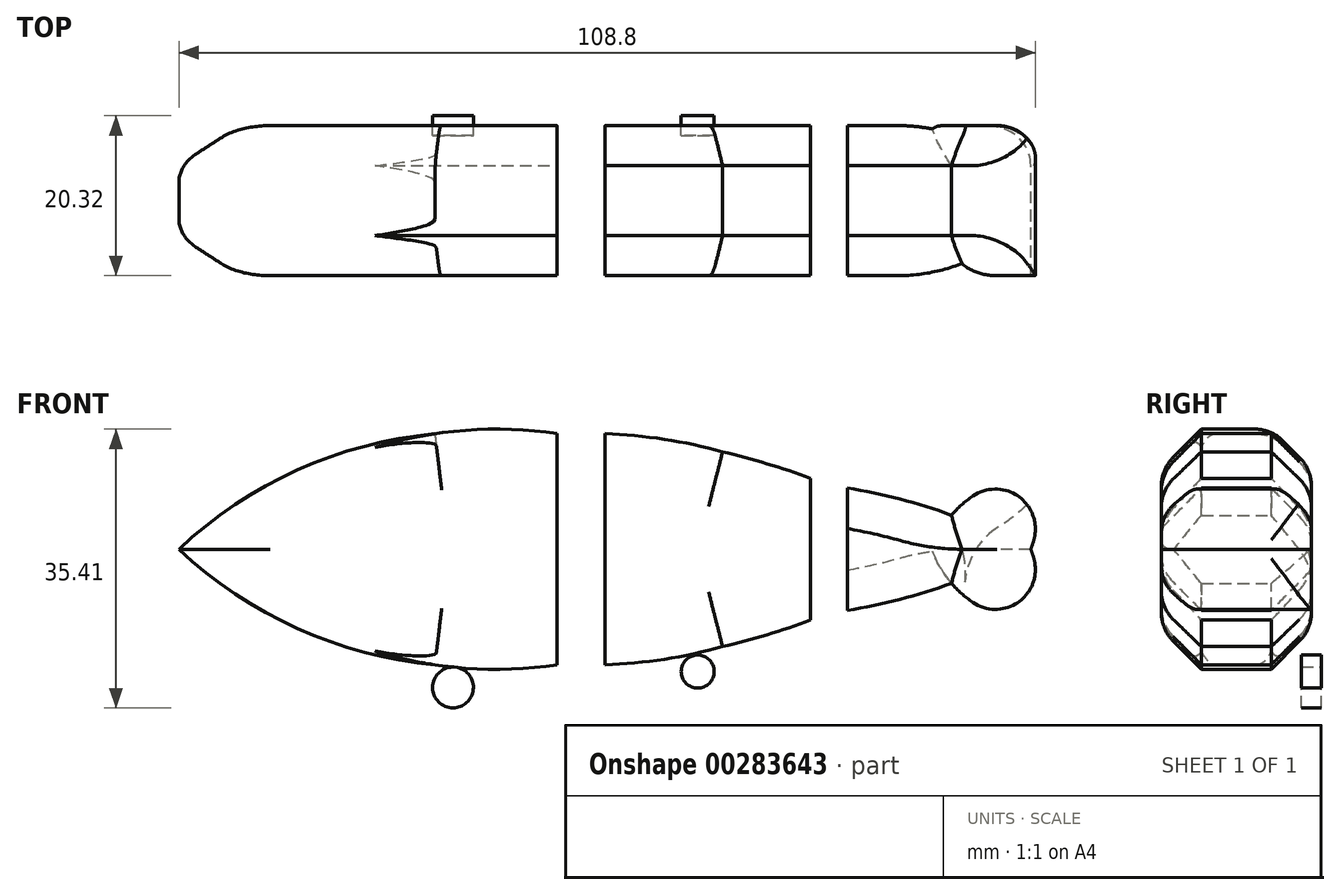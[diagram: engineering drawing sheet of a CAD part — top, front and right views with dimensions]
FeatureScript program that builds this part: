
annotation { "Feature Type Name" : "Feature", "Feature Type Description" : "" }
export const myFeature = defineFeature(function(context is Context, id is Id, definition is map)
    precondition{}
    {
        {
            var Q0;
            Q0=qCreatedBy(makeId("Front.planeOp"),FACE);
            var sketch = newSketch(context, id + "F0", { "sketchPlane" : qUnion([Q0])});
            skArc(sketch, "E0", {"start": v(-18.42, 14.68) * mm, "mid": v(-35.9, 10.05) * mm, "end": v(-50.94, 0) * mm});
            skArc(sketch, "E1", {"start": v(-2.88, 14.68) * mm, "mid": v(-10.65, 15.26) * mm, "end": v(-18.42, 14.68) * mm});
            skArc(sketch, "E2", {"start": v(18.13, 12.38) * mm, "mid": v(10.72, 13.97) * mm, "end": v(3.17, 14.68) * mm});
            skArc(sketch, "E3", {"start": v(29.31, 9) * mm, "mid": v(23.77, 10.86) * mm, "end": v(18.13, 12.38) * mm});
            skLineSegment(sketch, "E4", {"start": v(-2.88, 14.68) * mm, "end": v(-2.88, 0) * mm});
            skLineSegment(sketch, "E5", {"start": v(3.17, 14.68) * mm, "end": v(3.17, 0) * mm});
            skArc(sketch, "E6.MirrorCS", {"start": v(-18.42, -14.68) * mm, "mid": v(-35.9, -10.05) * mm, "end": v(-50.94, 0) * mm});
            skArc(sketch, "E7.MirrorCS", {"start": v(-2.88, -14.68) * mm, "mid": v(-10.65, -15.26) * mm, "end": v(-18.42, -14.68) * mm});
            skLineSegment(sketch, "E8.MirrorCS", {"start": v(-2.88, -14.68) * mm, "end": v(-2.88, 0) * mm});
            skLineSegment(sketch, "E9.MirrorCS", {"start": v(3.17, -14.68) * mm, "end": v(3.17, 0) * mm});
            skArc(sketch, "E10.MirrorCS", {"start": v(18.13, -12.38) * mm, "mid": v(10.72, -13.97) * mm, "end": v(3.17, -14.68) * mm});
            skArc(sketch, "E11.MirrorCS", {"start": v(29.31, -9) * mm, "mid": v(23.77, -10.86) * mm, "end": v(18.13, -12.38) * mm});
            skLineSegment(sketch, "E12", {"start": v(29.31, 9) * mm, "end": v(29.31, -9) * mm});
            skPoint(sketch, "E13.orphan", {"position": v(40, 4.32) * mm});
            skPoint(sketch, "E14.orphan", {"position": v(40, -4.32) * mm});
            skArc(sketch, "E15", {"start": v(47.2, 4.32) * mm, "mid": v(40.67, 6.37) * mm, "end": v(33.96, 7.77) * mm});
            skLineSegment(sketch, "E16", {"start": v(33.96, 7.77) * mm, "end": v(33.96, 0) * mm});
            skArc(sketch, "E17", {"start": v(57.27, 9.2) * mm, "mid": v(51.73, 7.81) * mm, "end": v(47.2, 4.32) * mm});
            skArc(sketch, "E18", {"start": v(57.27, 0) * mm, "mid": v(58.14, 4.6) * mm, "end": v(57.27, 9.2) * mm});
            skArc(sketch, "E19.MirrorCS", {"start": v(47.2, -4.32) * mm, "mid": v(40.67, -6.37) * mm, "end": v(33.96, -7.77) * mm});
            skLineSegment(sketch, "E20.MirrorCS", {"start": v(33.96, -7.77) * mm, "end": v(33.96, 0) * mm});
            skArc(sketch, "E21.MirrorCS", {"start": v(57.27, -9.2) * mm, "mid": v(51.73, -7.81) * mm, "end": v(47.2, -4.32) * mm});
            skArc(sketch, "E22.MirrorCS", {"start": v(57.27, 0) * mm, "mid": v(58.14, -4.6) * mm, "end": v(57.27, -9.2) * mm});
            skSolve(sketch);
        }
        {
            var Q0;
            Q0=makeQuery(id+"F0.imprint","IMPRINT",FACE,{"disambiguationData":[TD([[makeQuery(id+"F0.imprint","IMPRINT",EDGE,{"derivedFrom":sQuery(id+"F0.wireOp",EDGE,"E2")}),1.0]])]});
            var Q1;
            Q1=makeQuery(id+"F0.imprint","IMPRINT",FACE,{"disambiguationData":[TD([[makeQuery(id+"F0.imprint","IMPRINT",EDGE,{"derivedFrom":sQuery(id+"F0.wireOp",EDGE,"E15")}),1.0]])]});
            var Q2;
            Q2=makeQuery(id+"F0.imprint","IMPRINT",FACE,{"disambiguationData":[TD([[makeQuery(id+"F0.imprint","IMPRINT",EDGE,{"derivedFrom":sQuery(id+"F0.wireOp",EDGE,"E0")}),1.0]])]});
            extrude(context, id + "F1", {"entities" : qUnion([Q0, Q1, Q2]), "depth" : 19.05 * mm});
        }
        {
            var Q0;
            Q0=makeQuery(id+"F1.opExtrude","CAP_EDGE",EDGE,{"disambiguationData":[OSD([sQuery(id+"F0.wireOp",EDGE,"E0")])],"isStart":false});
            var Q1;
            Q1=makeQuery(id+"F1.opExtrude","CAP_EDGE",EDGE,{"disambiguationData":[OSD([sQuery(id+"F0.wireOp",EDGE,"E1")])],"isStart":false});
            var Q2;
            Q2=makeQuery(id+"F1.opExtrude","CAP_EDGE",EDGE,{"disambiguationData":[OSD([sQuery(id+"F0.wireOp",EDGE,"E6.MirrorCS")])],"isStart":false});
            var Q3;
            Q3=makeQuery(id+"F1.opExtrude","CAP_EDGE",EDGE,{"disambiguationData":[OSD([sQuery(id+"F0.wireOp",EDGE,"E7.MirrorCS")])],"isStart":false});
            var Q4;
            Q4=makeQuery(id+"F1.opExtrude","CAP_EDGE",EDGE,{"disambiguationData":[OSD([sQuery(id+"F0.wireOp",EDGE,"E1")])],"isStart":true});
            var Q5;
            Q5=makeQuery(id+"F1.opExtrude","CAP_EDGE",EDGE,{"disambiguationData":[OSD([sQuery(id+"F0.wireOp",EDGE,"E2")])],"isStart":true});
            var Q6;
            Q6=makeQuery(id+"F1.opExtrude","CAP_EDGE",EDGE,{"disambiguationData":[OSD([sQuery(id+"F0.wireOp",EDGE,"E3")])],"isStart":false});
            var Q7;
            Q7=makeQuery(id+"F1.opExtrude","CAP_EDGE",EDGE,{"disambiguationData":[OSD([sQuery(id+"F0.wireOp",EDGE,"E2")])],"isStart":false});
            var Q8;
            Q8=makeQuery(id+"F1.opExtrude","CAP_EDGE",EDGE,{"disambiguationData":[OSD([sQuery(id+"F0.wireOp",EDGE,"E15")])],"isStart":false});
            var Q9;
            Q9=makeQuery(id+"F1.opExtrude","CAP_EDGE",EDGE,{"disambiguationData":[OSD([sQuery(id+"F0.wireOp",EDGE,"E15")])],"isStart":true});
            var Q10;
            Q10=makeQuery(id+"F1.opExtrude","CAP_EDGE",EDGE,{"disambiguationData":[OSD([sQuery(id+"F0.wireOp",EDGE,"E17")])],"isStart":true});
            var Q11;
            Q11=makeQuery(id+"F1.opExtrude","CAP_EDGE",EDGE,{"disambiguationData":[OSD([sQuery(id+"F0.wireOp",EDGE,"E17")])],"isStart":false});
            var Q12;
            Q12=makeQuery(id+"F1.opExtrude","CAP_EDGE",EDGE,{"disambiguationData":[OSD([sQuery(id+"F0.wireOp",EDGE,"E21.MirrorCS")])],"isStart":false});
            var Q13;
            Q13=makeQuery(id+"F1.opExtrude","CAP_EDGE",EDGE,{"disambiguationData":[OSD([sQuery(id+"F0.wireOp",EDGE,"E19.MirrorCS")])],"isStart":false});
            var Q14;
            Q14=makeQuery(id+"F1.opExtrude","CAP_EDGE",EDGE,{"disambiguationData":[OSD([sQuery(id+"F0.wireOp",EDGE,"E10.MirrorCS")])],"isStart":false});
            var Q15;
            Q15=makeQuery(id+"F1.opExtrude","CAP_EDGE",EDGE,{"disambiguationData":[OSD([sQuery(id+"F0.wireOp",EDGE,"E19.MirrorCS")])],"isStart":true});
            var Q16;
            Q16=makeQuery(id+"F1.opExtrude","CAP_EDGE",EDGE,{"disambiguationData":[OSD([sQuery(id+"F0.wireOp",EDGE,"E6.MirrorCS")])],"isStart":true});
            var Q17;
            Q17=makeQuery(id+"F1.opExtrude","CAP_EDGE",EDGE,{"disambiguationData":[OSD([sQuery(id+"F0.wireOp",EDGE,"E7.MirrorCS")])],"isStart":true});
            var Q18;
            Q18=makeQuery(id+"F1.opExtrude","CAP_EDGE",EDGE,{"disambiguationData":[OSD([sQuery(id+"F0.wireOp",EDGE,"E10.MirrorCS")])],"isStart":true});
            chamfer(context, id + "F2", {"entities" : qUnion([Q0, Q1, Q2, Q3, Q4, Q5, Q6, Q7, Q8, Q9, Q10, Q11, Q12, Q13, Q14, Q15, Q16, Q17, Q18]), "width" : 5.08 * mm, "tangentPropagation" : true});
        }
        {
            var Q0;
            {var subQ0=sQuery(id+"F0.wireOp",EDGE,"E0");Q0=makeQuery(id+"F2.opChamfer","BLEND_EDGE",EDGE,{"blendedFrom":[makeQuery(id+"F1.opExtrude","CAP_EDGE",EDGE,{"disambiguationData":[OSD([subQ0])],"isStart":false}),makeQuery(id+"F1.opExtrude","CAP_FACE",FACE,{"disambiguationData":[OSD([subQ0,sQuery(id+"F0.wireOp",EDGE,"E1"),sQuery(id+"F0.wireOp",EDGE,"E4"),sQuery(id+"F0.wireOp",EDGE,"E6.MirrorCS"),sQuery(id+"F0.wireOp",EDGE,"E7.MirrorCS"),sQuery(id+"F0.wireOp",EDGE,"E8.MirrorCS")])],"isStart":false})],"blendedInto":[makeQuery(id+"F1.opExtrude","CAP_FACE",FACE,{"disambiguationData":[OSD([subQ0,sQuery(id+"F0.wireOp",EDGE,"E1"),sQuery(id+"F0.wireOp",EDGE,"E4"),sQuery(id+"F0.wireOp",EDGE,"E6.MirrorCS"),sQuery(id+"F0.wireOp",EDGE,"E7.MirrorCS"),sQuery(id+"F0.wireOp",EDGE,"E8.MirrorCS")])],"isStart":false})]});}
            var Q1;
            {var subQ0=sQuery(id+"F0.wireOp",EDGE,"E1");Q1=makeQuery(id+"F2.opChamfer","BLEND_EDGE",EDGE,{"blendedFrom":[makeQuery(id+"F1.opExtrude","CAP_EDGE",EDGE,{"disambiguationData":[OSD([subQ0])],"isStart":false}),makeQuery(id+"F1.opExtrude","CAP_FACE",FACE,{"disambiguationData":[OSD([sQuery(id+"F0.wireOp",EDGE,"E0"),subQ0,sQuery(id+"F0.wireOp",EDGE,"E4"),sQuery(id+"F0.wireOp",EDGE,"E6.MirrorCS"),sQuery(id+"F0.wireOp",EDGE,"E7.MirrorCS"),sQuery(id+"F0.wireOp",EDGE,"E8.MirrorCS")])],"isStart":false})],"blendedInto":[makeQuery(id+"F1.opExtrude","CAP_FACE",FACE,{"disambiguationData":[OSD([sQuery(id+"F0.wireOp",EDGE,"E0"),subQ0,sQuery(id+"F0.wireOp",EDGE,"E4"),sQuery(id+"F0.wireOp",EDGE,"E6.MirrorCS"),sQuery(id+"F0.wireOp",EDGE,"E7.MirrorCS"),sQuery(id+"F0.wireOp",EDGE,"E8.MirrorCS")])],"isStart":false})]});}
            var Q2;
            {var subQ0=sQuery(id+"F0.wireOp",EDGE,"E6.MirrorCS");Q2=makeQuery(id+"F2.opChamfer","BLEND_EDGE",EDGE,{"blendedFrom":[makeQuery(id+"F1.opExtrude","CAP_EDGE",EDGE,{"disambiguationData":[OSD([subQ0])],"isStart":false}),makeQuery(id+"F1.opExtrude","CAP_FACE",FACE,{"disambiguationData":[OSD([sQuery(id+"F0.wireOp",EDGE,"E0"),sQuery(id+"F0.wireOp",EDGE,"E1"),sQuery(id+"F0.wireOp",EDGE,"E4"),subQ0,sQuery(id+"F0.wireOp",EDGE,"E7.MirrorCS"),sQuery(id+"F0.wireOp",EDGE,"E8.MirrorCS")])],"isStart":false})],"blendedInto":[makeQuery(id+"F1.opExtrude","CAP_FACE",FACE,{"disambiguationData":[OSD([sQuery(id+"F0.wireOp",EDGE,"E0"),sQuery(id+"F0.wireOp",EDGE,"E1"),sQuery(id+"F0.wireOp",EDGE,"E4"),subQ0,sQuery(id+"F0.wireOp",EDGE,"E7.MirrorCS"),sQuery(id+"F0.wireOp",EDGE,"E8.MirrorCS")])],"isStart":false})]});}
            var Q3;
            {var subQ0=sQuery(id+"F0.wireOp",EDGE,"E7.MirrorCS");Q3=makeQuery(id+"F2.opChamfer","BLEND_EDGE",EDGE,{"blendedFrom":[makeQuery(id+"F1.opExtrude","CAP_EDGE",EDGE,{"disambiguationData":[OSD([subQ0])],"isStart":false}),makeQuery(id+"F1.opExtrude","CAP_FACE",FACE,{"disambiguationData":[OSD([sQuery(id+"F0.wireOp",EDGE,"E0"),sQuery(id+"F0.wireOp",EDGE,"E1"),sQuery(id+"F0.wireOp",EDGE,"E4"),sQuery(id+"F0.wireOp",EDGE,"E6.MirrorCS"),subQ0,sQuery(id+"F0.wireOp",EDGE,"E8.MirrorCS")])],"isStart":false})],"blendedInto":[makeQuery(id+"F1.opExtrude","CAP_FACE",FACE,{"disambiguationData":[OSD([sQuery(id+"F0.wireOp",EDGE,"E0"),sQuery(id+"F0.wireOp",EDGE,"E1"),sQuery(id+"F0.wireOp",EDGE,"E4"),sQuery(id+"F0.wireOp",EDGE,"E6.MirrorCS"),subQ0,sQuery(id+"F0.wireOp",EDGE,"E8.MirrorCS")])],"isStart":false})]});}
            var Q4;
            {var subQ0=sQuery(id+"F0.wireOp",EDGE,"E11.MirrorCS");Q4=makeQuery(id+"F2.opChamfer","BLEND_EDGE",EDGE,{"blendedFrom":[makeQuery(id+"F1.opExtrude","CAP_EDGE",EDGE,{"disambiguationData":[OSD([subQ0])],"isStart":false}),makeQuery(id+"F1.opExtrude","CAP_FACE",FACE,{"disambiguationData":[OSD([sQuery(id+"F0.wireOp",EDGE,"E2"),sQuery(id+"F0.wireOp",EDGE,"E3"),sQuery(id+"F0.wireOp",EDGE,"E5"),sQuery(id+"F0.wireOp",EDGE,"E9.MirrorCS"),sQuery(id+"F0.wireOp",EDGE,"E10.MirrorCS"),subQ0,sQuery(id+"F0.wireOp",EDGE,"E12")])],"isStart":false})],"blendedInto":[makeQuery(id+"F1.opExtrude","CAP_FACE",FACE,{"disambiguationData":[OSD([sQuery(id+"F0.wireOp",EDGE,"E2"),sQuery(id+"F0.wireOp",EDGE,"E3"),sQuery(id+"F0.wireOp",EDGE,"E5"),sQuery(id+"F0.wireOp",EDGE,"E9.MirrorCS"),sQuery(id+"F0.wireOp",EDGE,"E10.MirrorCS"),subQ0,sQuery(id+"F0.wireOp",EDGE,"E12")])],"isStart":false})]});}
            var Q5;
            {var subQ0=sQuery(id+"F0.wireOp",EDGE,"E3");Q5=makeQuery(id+"F2.opChamfer","BLEND_EDGE",EDGE,{"blendedFrom":[makeQuery(id+"F1.opExtrude","CAP_EDGE",EDGE,{"disambiguationData":[OSD([subQ0])],"isStart":false}),makeQuery(id+"F1.opExtrude","CAP_FACE",FACE,{"disambiguationData":[OSD([sQuery(id+"F0.wireOp",EDGE,"E2"),subQ0,sQuery(id+"F0.wireOp",EDGE,"E5"),sQuery(id+"F0.wireOp",EDGE,"E9.MirrorCS"),sQuery(id+"F0.wireOp",EDGE,"E10.MirrorCS"),sQuery(id+"F0.wireOp",EDGE,"E11.MirrorCS"),sQuery(id+"F0.wireOp",EDGE,"E12")])],"isStart":false})],"blendedInto":[makeQuery(id+"F1.opExtrude","CAP_FACE",FACE,{"disambiguationData":[OSD([sQuery(id+"F0.wireOp",EDGE,"E2"),subQ0,sQuery(id+"F0.wireOp",EDGE,"E5"),sQuery(id+"F0.wireOp",EDGE,"E9.MirrorCS"),sQuery(id+"F0.wireOp",EDGE,"E10.MirrorCS"),sQuery(id+"F0.wireOp",EDGE,"E11.MirrorCS"),sQuery(id+"F0.wireOp",EDGE,"E12")])],"isStart":false})]});}
            var Q6;
            {var subQ0=sQuery(id+"F0.wireOp",EDGE,"E2");Q6=makeQuery(id+"F2.opChamfer","BLEND_EDGE",EDGE,{"blendedFrom":[makeQuery(id+"F1.opExtrude","CAP_EDGE",EDGE,{"disambiguationData":[OSD([subQ0])],"isStart":false}),makeQuery(id+"F1.opExtrude","CAP_FACE",FACE,{"disambiguationData":[OSD([subQ0,sQuery(id+"F0.wireOp",EDGE,"E3"),sQuery(id+"F0.wireOp",EDGE,"E5"),sQuery(id+"F0.wireOp",EDGE,"E9.MirrorCS"),sQuery(id+"F0.wireOp",EDGE,"E10.MirrorCS"),sQuery(id+"F0.wireOp",EDGE,"E11.MirrorCS"),sQuery(id+"F0.wireOp",EDGE,"E12")])],"isStart":false})],"blendedInto":[makeQuery(id+"F1.opExtrude","CAP_FACE",FACE,{"disambiguationData":[OSD([subQ0,sQuery(id+"F0.wireOp",EDGE,"E3"),sQuery(id+"F0.wireOp",EDGE,"E5"),sQuery(id+"F0.wireOp",EDGE,"E9.MirrorCS"),sQuery(id+"F0.wireOp",EDGE,"E10.MirrorCS"),sQuery(id+"F0.wireOp",EDGE,"E11.MirrorCS"),sQuery(id+"F0.wireOp",EDGE,"E12")])],"isStart":false})]});}
            var Q7;
            {var subQ0=sQuery(id+"F0.wireOp",EDGE,"E10.MirrorCS");Q7=makeQuery(id+"F2.opChamfer","BLEND_EDGE",EDGE,{"blendedFrom":[makeQuery(id+"F1.opExtrude","CAP_EDGE",EDGE,{"disambiguationData":[OSD([subQ0])],"isStart":false}),makeQuery(id+"F1.opExtrude","CAP_FACE",FACE,{"disambiguationData":[OSD([sQuery(id+"F0.wireOp",EDGE,"E2"),sQuery(id+"F0.wireOp",EDGE,"E3"),sQuery(id+"F0.wireOp",EDGE,"E5"),sQuery(id+"F0.wireOp",EDGE,"E9.MirrorCS"),subQ0,sQuery(id+"F0.wireOp",EDGE,"E11.MirrorCS"),sQuery(id+"F0.wireOp",EDGE,"E12")])],"isStart":false})],"blendedInto":[makeQuery(id+"F1.opExtrude","CAP_FACE",FACE,{"disambiguationData":[OSD([sQuery(id+"F0.wireOp",EDGE,"E2"),sQuery(id+"F0.wireOp",EDGE,"E3"),sQuery(id+"F0.wireOp",EDGE,"E5"),sQuery(id+"F0.wireOp",EDGE,"E9.MirrorCS"),subQ0,sQuery(id+"F0.wireOp",EDGE,"E11.MirrorCS"),sQuery(id+"F0.wireOp",EDGE,"E12")])],"isStart":false})]});}
            var Q8;
            {var subQ0=sQuery(id+"F0.wireOp",EDGE,"E19.MirrorCS");Q8=makeQuery(id+"F2.opChamfer","BLEND_EDGE",EDGE,{"blendedFrom":[makeQuery(id+"F1.opExtrude","CAP_EDGE",EDGE,{"disambiguationData":[OSD([subQ0])],"isStart":false}),makeQuery(id+"F1.opExtrude","CAP_FACE",FACE,{"disambiguationData":[OSD([sQuery(id+"F0.wireOp",EDGE,"E15"),sQuery(id+"F0.wireOp",EDGE,"E16"),sQuery(id+"F0.wireOp",EDGE,"E17"),sQuery(id+"F0.wireOp",EDGE,"E18"),subQ0,sQuery(id+"F0.wireOp",EDGE,"E20.MirrorCS"),sQuery(id+"F0.wireOp",EDGE,"E21.MirrorCS"),sQuery(id+"F0.wireOp",EDGE,"E22.MirrorCS")])],"isStart":false})],"blendedInto":[makeQuery(id+"F1.opExtrude","CAP_FACE",FACE,{"disambiguationData":[OSD([sQuery(id+"F0.wireOp",EDGE,"E15"),sQuery(id+"F0.wireOp",EDGE,"E16"),sQuery(id+"F0.wireOp",EDGE,"E17"),sQuery(id+"F0.wireOp",EDGE,"E18"),subQ0,sQuery(id+"F0.wireOp",EDGE,"E20.MirrorCS"),sQuery(id+"F0.wireOp",EDGE,"E21.MirrorCS"),sQuery(id+"F0.wireOp",EDGE,"E22.MirrorCS")])],"isStart":false})]});}
            var Q9;
            {var subQ0=sQuery(id+"F0.wireOp",EDGE,"E17");Q9=makeQuery(id+"F2.opChamfer","BLEND_EDGE",EDGE,{"blendedFrom":[makeQuery(id+"F1.opExtrude","CAP_EDGE",EDGE,{"disambiguationData":[OSD([subQ0])],"isStart":false}),makeQuery(id+"F1.opExtrude","CAP_FACE",FACE,{"disambiguationData":[OSD([sQuery(id+"F0.wireOp",EDGE,"E15"),sQuery(id+"F0.wireOp",EDGE,"E16"),subQ0,sQuery(id+"F0.wireOp",EDGE,"E18"),sQuery(id+"F0.wireOp",EDGE,"E19.MirrorCS"),sQuery(id+"F0.wireOp",EDGE,"E20.MirrorCS"),sQuery(id+"F0.wireOp",EDGE,"E21.MirrorCS"),sQuery(id+"F0.wireOp",EDGE,"E22.MirrorCS")])],"isStart":false})],"blendedInto":[makeQuery(id+"F1.opExtrude","CAP_FACE",FACE,{"disambiguationData":[OSD([sQuery(id+"F0.wireOp",EDGE,"E15"),sQuery(id+"F0.wireOp",EDGE,"E16"),subQ0,sQuery(id+"F0.wireOp",EDGE,"E18"),sQuery(id+"F0.wireOp",EDGE,"E19.MirrorCS"),sQuery(id+"F0.wireOp",EDGE,"E20.MirrorCS"),sQuery(id+"F0.wireOp",EDGE,"E21.MirrorCS"),sQuery(id+"F0.wireOp",EDGE,"E22.MirrorCS")])],"isStart":false})]});}
            var Q10;
            {var subQ0=sQuery(id+"F0.wireOp",EDGE,"E21.MirrorCS");Q10=makeQuery(id+"F2.opChamfer","BLEND_EDGE",EDGE,{"blendedFrom":[makeQuery(id+"F1.opExtrude","CAP_EDGE",EDGE,{"disambiguationData":[OSD([subQ0])],"isStart":false}),makeQuery(id+"F1.opExtrude","CAP_FACE",FACE,{"disambiguationData":[OSD([sQuery(id+"F0.wireOp",EDGE,"E15"),sQuery(id+"F0.wireOp",EDGE,"E16"),sQuery(id+"F0.wireOp",EDGE,"E17"),sQuery(id+"F0.wireOp",EDGE,"E18"),sQuery(id+"F0.wireOp",EDGE,"E19.MirrorCS"),sQuery(id+"F0.wireOp",EDGE,"E20.MirrorCS"),subQ0,sQuery(id+"F0.wireOp",EDGE,"E22.MirrorCS")])],"isStart":false})],"blendedInto":[makeQuery(id+"F1.opExtrude","CAP_FACE",FACE,{"disambiguationData":[OSD([sQuery(id+"F0.wireOp",EDGE,"E15"),sQuery(id+"F0.wireOp",EDGE,"E16"),sQuery(id+"F0.wireOp",EDGE,"E17"),sQuery(id+"F0.wireOp",EDGE,"E18"),sQuery(id+"F0.wireOp",EDGE,"E19.MirrorCS"),sQuery(id+"F0.wireOp",EDGE,"E20.MirrorCS"),subQ0,sQuery(id+"F0.wireOp",EDGE,"E22.MirrorCS")])],"isStart":false})]});}
            var Q11;
            {var subQ0=sQuery(id+"F0.wireOp",EDGE,"E0");Q11=makeQuery(id+"F2.opChamfer","BLEND_EDGE",EDGE,{"blendedFrom":[makeQuery(id+"F1.opExtrude","CAP_EDGE",EDGE,{"disambiguationData":[OSD([subQ0])],"isStart":false}),makeQuery(id+"F1.opExtrude","SWEPT_FACE",FACE,{"disambiguationData":[OSD([subQ0])]})],"blendedInto":[makeQuery(id+"F1.opExtrude","SWEPT_FACE",FACE,{"disambiguationData":[OSD([subQ0])]})]});}
            var Q12;
            {var subQ0=sQuery(id+"F0.wireOp",EDGE,"E0");Q12=makeQuery(id+"F2.opChamfer","BLEND_EDGE",EDGE,{"blendedFrom":[makeQuery(id+"F1.opExtrude","CAP_EDGE",EDGE,{"disambiguationData":[OSD([subQ0])],"isStart":true}),makeQuery(id+"F1.opExtrude","SWEPT_FACE",FACE,{"disambiguationData":[OSD([subQ0])]})],"blendedInto":[makeQuery(id+"F1.opExtrude","SWEPT_FACE",FACE,{"disambiguationData":[OSD([subQ0])]})]});}
            var Q13;
            {var subQ0=sQuery(id+"F0.wireOp",EDGE,"E6.MirrorCS");Q13=makeQuery(id+"F2.opChamfer","BLEND_EDGE",EDGE,{"blendedFrom":[makeQuery(id+"F1.opExtrude","CAP_EDGE",EDGE,{"disambiguationData":[OSD([subQ0])],"isStart":true}),makeQuery(id+"F1.opExtrude","SWEPT_FACE",FACE,{"disambiguationData":[OSD([subQ0])]})],"blendedInto":[makeQuery(id+"F1.opExtrude","SWEPT_FACE",FACE,{"disambiguationData":[OSD([subQ0])]})]});}
            var Q14;
            {var subQ0=sQuery(id+"F0.wireOp",EDGE,"E6.MirrorCS");Q14=makeQuery(id+"F2.opChamfer","BLEND_EDGE",EDGE,{"blendedFrom":[makeQuery(id+"F1.opExtrude","CAP_EDGE",EDGE,{"disambiguationData":[OSD([subQ0])],"isStart":false}),makeQuery(id+"F1.opExtrude","SWEPT_FACE",FACE,{"disambiguationData":[OSD([subQ0])]})],"blendedInto":[makeQuery(id+"F1.opExtrude","SWEPT_FACE",FACE,{"disambiguationData":[OSD([subQ0])]})]});}
            var Q15;
            {var subQ0=sQuery(id+"F0.wireOp",EDGE,"E0");Q15=makeQuery(id+"F2.opChamfer","BLEND_EDGE",EDGE,{"blendedFrom":[makeQuery(id+"F1.opExtrude","CAP_EDGE",EDGE,{"disambiguationData":[OSD([subQ0])],"isStart":true}),makeQuery(id+"F1.opExtrude","CAP_FACE",FACE,{"disambiguationData":[OSD([subQ0,sQuery(id+"F0.wireOp",EDGE,"E1"),sQuery(id+"F0.wireOp",EDGE,"E4"),sQuery(id+"F0.wireOp",EDGE,"E6.MirrorCS"),sQuery(id+"F0.wireOp",EDGE,"E7.MirrorCS"),sQuery(id+"F0.wireOp",EDGE,"E8.MirrorCS")])],"isStart":true})],"blendedInto":[makeQuery(id+"F1.opExtrude","CAP_FACE",FACE,{"disambiguationData":[OSD([subQ0,sQuery(id+"F0.wireOp",EDGE,"E1"),sQuery(id+"F0.wireOp",EDGE,"E4"),sQuery(id+"F0.wireOp",EDGE,"E6.MirrorCS"),sQuery(id+"F0.wireOp",EDGE,"E7.MirrorCS"),sQuery(id+"F0.wireOp",EDGE,"E8.MirrorCS")])],"isStart":true})]});}
            var Q16;
            {var subQ0=sQuery(id+"F0.wireOp",EDGE,"E1");Q16=makeQuery(id+"F2.opChamfer","BLEND_EDGE",EDGE,{"blendedFrom":[makeQuery(id+"F1.opExtrude","CAP_EDGE",EDGE,{"disambiguationData":[OSD([subQ0])],"isStart":true}),makeQuery(id+"F1.opExtrude","CAP_FACE",FACE,{"disambiguationData":[OSD([sQuery(id+"F0.wireOp",EDGE,"E0"),subQ0,sQuery(id+"F0.wireOp",EDGE,"E4"),sQuery(id+"F0.wireOp",EDGE,"E6.MirrorCS"),sQuery(id+"F0.wireOp",EDGE,"E7.MirrorCS"),sQuery(id+"F0.wireOp",EDGE,"E8.MirrorCS")])],"isStart":true})],"blendedInto":[makeQuery(id+"F1.opExtrude","CAP_FACE",FACE,{"disambiguationData":[OSD([sQuery(id+"F0.wireOp",EDGE,"E0"),subQ0,sQuery(id+"F0.wireOp",EDGE,"E4"),sQuery(id+"F0.wireOp",EDGE,"E6.MirrorCS"),sQuery(id+"F0.wireOp",EDGE,"E7.MirrorCS"),sQuery(id+"F0.wireOp",EDGE,"E8.MirrorCS")])],"isStart":true})]});}
            var Q17;
            {var subQ0=sQuery(id+"F0.wireOp",EDGE,"E1");Q17=makeQuery(id+"F2.opChamfer","BLEND_EDGE",EDGE,{"blendedFrom":[makeQuery(id+"F1.opExtrude","CAP_EDGE",EDGE,{"disambiguationData":[OSD([subQ0])],"isStart":true}),makeQuery(id+"F1.opExtrude","SWEPT_FACE",FACE,{"disambiguationData":[OSD([subQ0])]})],"blendedInto":[makeQuery(id+"F1.opExtrude","SWEPT_FACE",FACE,{"disambiguationData":[OSD([subQ0])]})]});}
            var Q18;
            {var subQ0=sQuery(id+"F0.wireOp",EDGE,"E6.MirrorCS");Q18=makeQuery(id+"F2.opChamfer","BLEND_EDGE",EDGE,{"blendedFrom":[makeQuery(id+"F1.opExtrude","CAP_EDGE",EDGE,{"disambiguationData":[OSD([subQ0])],"isStart":true}),makeQuery(id+"F1.opExtrude","CAP_FACE",FACE,{"disambiguationData":[OSD([sQuery(id+"F0.wireOp",EDGE,"E0"),sQuery(id+"F0.wireOp",EDGE,"E1"),sQuery(id+"F0.wireOp",EDGE,"E4"),subQ0,sQuery(id+"F0.wireOp",EDGE,"E7.MirrorCS"),sQuery(id+"F0.wireOp",EDGE,"E8.MirrorCS")])],"isStart":true})],"blendedInto":[makeQuery(id+"F1.opExtrude","CAP_FACE",FACE,{"disambiguationData":[OSD([sQuery(id+"F0.wireOp",EDGE,"E0"),sQuery(id+"F0.wireOp",EDGE,"E1"),sQuery(id+"F0.wireOp",EDGE,"E4"),subQ0,sQuery(id+"F0.wireOp",EDGE,"E7.MirrorCS"),sQuery(id+"F0.wireOp",EDGE,"E8.MirrorCS")])],"isStart":true})]});}
            var Q19;
            {var subQ0=sQuery(id+"F0.wireOp",EDGE,"E7.MirrorCS");Q19=makeQuery(id+"F2.opChamfer","BLEND_EDGE",EDGE,{"blendedFrom":[makeQuery(id+"F1.opExtrude","CAP_EDGE",EDGE,{"disambiguationData":[OSD([subQ0])],"isStart":true}),makeQuery(id+"F1.opExtrude","CAP_FACE",FACE,{"disambiguationData":[OSD([sQuery(id+"F0.wireOp",EDGE,"E0"),sQuery(id+"F0.wireOp",EDGE,"E1"),sQuery(id+"F0.wireOp",EDGE,"E4"),sQuery(id+"F0.wireOp",EDGE,"E6.MirrorCS"),subQ0,sQuery(id+"F0.wireOp",EDGE,"E8.MirrorCS")])],"isStart":true})],"blendedInto":[makeQuery(id+"F1.opExtrude","CAP_FACE",FACE,{"disambiguationData":[OSD([sQuery(id+"F0.wireOp",EDGE,"E0"),sQuery(id+"F0.wireOp",EDGE,"E1"),sQuery(id+"F0.wireOp",EDGE,"E4"),sQuery(id+"F0.wireOp",EDGE,"E6.MirrorCS"),subQ0,sQuery(id+"F0.wireOp",EDGE,"E8.MirrorCS")])],"isStart":true})]});}
            var Q20;
            {var subQ0=sQuery(id+"F0.wireOp",EDGE,"E2");Q20=makeQuery(id+"F2.opChamfer","BLEND_EDGE",EDGE,{"blendedFrom":[makeQuery(id+"F1.opExtrude","CAP_EDGE",EDGE,{"disambiguationData":[OSD([subQ0])],"isStart":true}),makeQuery(id+"F1.opExtrude","CAP_FACE",FACE,{"disambiguationData":[OSD([subQ0,sQuery(id+"F0.wireOp",EDGE,"E3"),sQuery(id+"F0.wireOp",EDGE,"E5"),sQuery(id+"F0.wireOp",EDGE,"E9.MirrorCS"),sQuery(id+"F0.wireOp",EDGE,"E10.MirrorCS"),sQuery(id+"F0.wireOp",EDGE,"E11.MirrorCS"),sQuery(id+"F0.wireOp",EDGE,"E12")])],"isStart":true})],"blendedInto":[makeQuery(id+"F1.opExtrude","CAP_FACE",FACE,{"disambiguationData":[OSD([subQ0,sQuery(id+"F0.wireOp",EDGE,"E3"),sQuery(id+"F0.wireOp",EDGE,"E5"),sQuery(id+"F0.wireOp",EDGE,"E9.MirrorCS"),sQuery(id+"F0.wireOp",EDGE,"E10.MirrorCS"),sQuery(id+"F0.wireOp",EDGE,"E11.MirrorCS"),sQuery(id+"F0.wireOp",EDGE,"E12")])],"isStart":true})]});}
            var Q21;
            {var subQ0=sQuery(id+"F0.wireOp",EDGE,"E3");Q21=makeQuery(id+"F2.opChamfer","BLEND_EDGE",EDGE,{"blendedFrom":[makeQuery(id+"F1.opExtrude","CAP_EDGE",EDGE,{"disambiguationData":[OSD([subQ0])],"isStart":true}),makeQuery(id+"F1.opExtrude","CAP_FACE",FACE,{"disambiguationData":[OSD([sQuery(id+"F0.wireOp",EDGE,"E2"),subQ0,sQuery(id+"F0.wireOp",EDGE,"E5"),sQuery(id+"F0.wireOp",EDGE,"E9.MirrorCS"),sQuery(id+"F0.wireOp",EDGE,"E10.MirrorCS"),sQuery(id+"F0.wireOp",EDGE,"E11.MirrorCS"),sQuery(id+"F0.wireOp",EDGE,"E12")])],"isStart":true})],"blendedInto":[makeQuery(id+"F1.opExtrude","CAP_FACE",FACE,{"disambiguationData":[OSD([sQuery(id+"F0.wireOp",EDGE,"E2"),subQ0,sQuery(id+"F0.wireOp",EDGE,"E5"),sQuery(id+"F0.wireOp",EDGE,"E9.MirrorCS"),sQuery(id+"F0.wireOp",EDGE,"E10.MirrorCS"),sQuery(id+"F0.wireOp",EDGE,"E11.MirrorCS"),sQuery(id+"F0.wireOp",EDGE,"E12")])],"isStart":true})]});}
            var Q22;
            {var subQ0=sQuery(id+"F0.wireOp",EDGE,"E11.MirrorCS");Q22=makeQuery(id+"F2.opChamfer","BLEND_EDGE",EDGE,{"blendedFrom":[makeQuery(id+"F1.opExtrude","CAP_EDGE",EDGE,{"disambiguationData":[OSD([subQ0])],"isStart":true}),makeQuery(id+"F1.opExtrude","CAP_FACE",FACE,{"disambiguationData":[OSD([sQuery(id+"F0.wireOp",EDGE,"E2"),sQuery(id+"F0.wireOp",EDGE,"E3"),sQuery(id+"F0.wireOp",EDGE,"E5"),sQuery(id+"F0.wireOp",EDGE,"E9.MirrorCS"),sQuery(id+"F0.wireOp",EDGE,"E10.MirrorCS"),subQ0,sQuery(id+"F0.wireOp",EDGE,"E12")])],"isStart":true})],"blendedInto":[makeQuery(id+"F1.opExtrude","CAP_FACE",FACE,{"disambiguationData":[OSD([sQuery(id+"F0.wireOp",EDGE,"E2"),sQuery(id+"F0.wireOp",EDGE,"E3"),sQuery(id+"F0.wireOp",EDGE,"E5"),sQuery(id+"F0.wireOp",EDGE,"E9.MirrorCS"),sQuery(id+"F0.wireOp",EDGE,"E10.MirrorCS"),subQ0,sQuery(id+"F0.wireOp",EDGE,"E12")])],"isStart":true})]});}
            var Q23;
            {var subQ0=sQuery(id+"F0.wireOp",EDGE,"E10.MirrorCS");Q23=makeQuery(id+"F2.opChamfer","BLEND_EDGE",EDGE,{"blendedFrom":[makeQuery(id+"F1.opExtrude","CAP_EDGE",EDGE,{"disambiguationData":[OSD([subQ0])],"isStart":true}),makeQuery(id+"F1.opExtrude","CAP_FACE",FACE,{"disambiguationData":[OSD([sQuery(id+"F0.wireOp",EDGE,"E2"),sQuery(id+"F0.wireOp",EDGE,"E3"),sQuery(id+"F0.wireOp",EDGE,"E5"),sQuery(id+"F0.wireOp",EDGE,"E9.MirrorCS"),subQ0,sQuery(id+"F0.wireOp",EDGE,"E11.MirrorCS"),sQuery(id+"F0.wireOp",EDGE,"E12")])],"isStart":true})],"blendedInto":[makeQuery(id+"F1.opExtrude","CAP_FACE",FACE,{"disambiguationData":[OSD([sQuery(id+"F0.wireOp",EDGE,"E2"),sQuery(id+"F0.wireOp",EDGE,"E3"),sQuery(id+"F0.wireOp",EDGE,"E5"),sQuery(id+"F0.wireOp",EDGE,"E9.MirrorCS"),subQ0,sQuery(id+"F0.wireOp",EDGE,"E11.MirrorCS"),sQuery(id+"F0.wireOp",EDGE,"E12")])],"isStart":true})]});}
            var Q24;
            {var subQ0=sQuery(id+"F0.wireOp",EDGE,"E15");Q24=makeQuery(id+"F2.opChamfer","BLEND_EDGE",EDGE,{"disambiguationData":[OD(1.0)],"blendedFrom":[makeQuery(id+"F1.opExtrude","CAP_EDGE",EDGE,{"disambiguationData":[OSD([subQ0])],"isStart":true}),makeQuery(id+"F1.opExtrude","CAP_FACE",FACE,{"disambiguationData":[OSD([subQ0,sQuery(id+"F0.wireOp",EDGE,"E16"),sQuery(id+"F0.wireOp",EDGE,"E17"),sQuery(id+"F0.wireOp",EDGE,"E18"),sQuery(id+"F0.wireOp",EDGE,"E19.MirrorCS"),sQuery(id+"F0.wireOp",EDGE,"E20.MirrorCS"),sQuery(id+"F0.wireOp",EDGE,"E21.MirrorCS"),sQuery(id+"F0.wireOp",EDGE,"E22.MirrorCS")])],"isStart":true})],"blendedInto":[makeQuery(id+"F1.opExtrude","CAP_FACE",FACE,{"disambiguationData":[OSD([subQ0,sQuery(id+"F0.wireOp",EDGE,"E16"),sQuery(id+"F0.wireOp",EDGE,"E17"),sQuery(id+"F0.wireOp",EDGE,"E18"),sQuery(id+"F0.wireOp",EDGE,"E19.MirrorCS"),sQuery(id+"F0.wireOp",EDGE,"E20.MirrorCS"),sQuery(id+"F0.wireOp",EDGE,"E21.MirrorCS"),sQuery(id+"F0.wireOp",EDGE,"E22.MirrorCS")])],"isStart":true})]});}
            var Q25;
            Q25=makeQuery(id+"F1.opExtrude","SWEPT_EDGE",EDGE,{"disambiguationData":[OSD([sQuery(id+"F0.wireOp",EDGE,"E21.MirrorCS"),sQuery(id+"F0.wireOp",EDGE,"E22.MirrorCS")])]});
            var Q26;
            Q26=makeQuery(id+"F1.opExtrude","SWEPT_EDGE",EDGE,{"disambiguationData":[OSD([sQuery(id+"F0.wireOp",EDGE,"E17"),sQuery(id+"F0.wireOp",EDGE,"E18")])]});
            var Q27;
            Q27=makeQuery(id+"F1.opExtrude","CAP_EDGE",EDGE,{"disambiguationData":[OSD([sQuery(id+"F0.wireOp",EDGE,"E18")])],"isStart":true});
            var Q28;
            Q28=makeQuery(id+"F1.opExtrude","CAP_EDGE",EDGE,{"disambiguationData":[OSD([sQuery(id+"F0.wireOp",EDGE,"E22.MirrorCS")])],"isStart":true});
            fillet(context, id + "F3", {"entities" : qUnion([Q0, Q1, Q2, Q3, Q4, Q5, Q6, Q7, Q8, Q9, Q10, Q11, Q12, Q13, Q14, Q15, Q16, Q17, Q18, Q19, Q20, Q21, Q22, Q23, Q24, Q25, Q26, Q27, Q28]), "radius" : 5.08 * mm, "tangentPropagation" : true, "allowEdgeOverflow" : false});
        }
        {
            var Q0;
            Q0=qCreatedBy(makeId("Front.planeOp"),FACE);
            var sketch = newSketch(context, id + "F4", { "sketchPlane" : qUnion([Q0])});
            skCircle(sketch, "E23", {"center": v(-16.12, -17.56) * mm, "radius": 2.6 * mm});
            skCircle(sketch, "E24", {"center": v(14.97, -15.54) * mm, "radius": 2.1 * mm});
            skSolve(sketch);
        }
        {
            var Q0;
            Q0 = qSketchRegion(id + "F4", true);
            extrude(context, id + "F5", {"entities" : qUnion([Q0]), "operationType" : NewBodyOperationType.ADD, "endBound" : BoundingType.SYMMETRIC, "depth" : 2.54 * mm});
        }
    });
